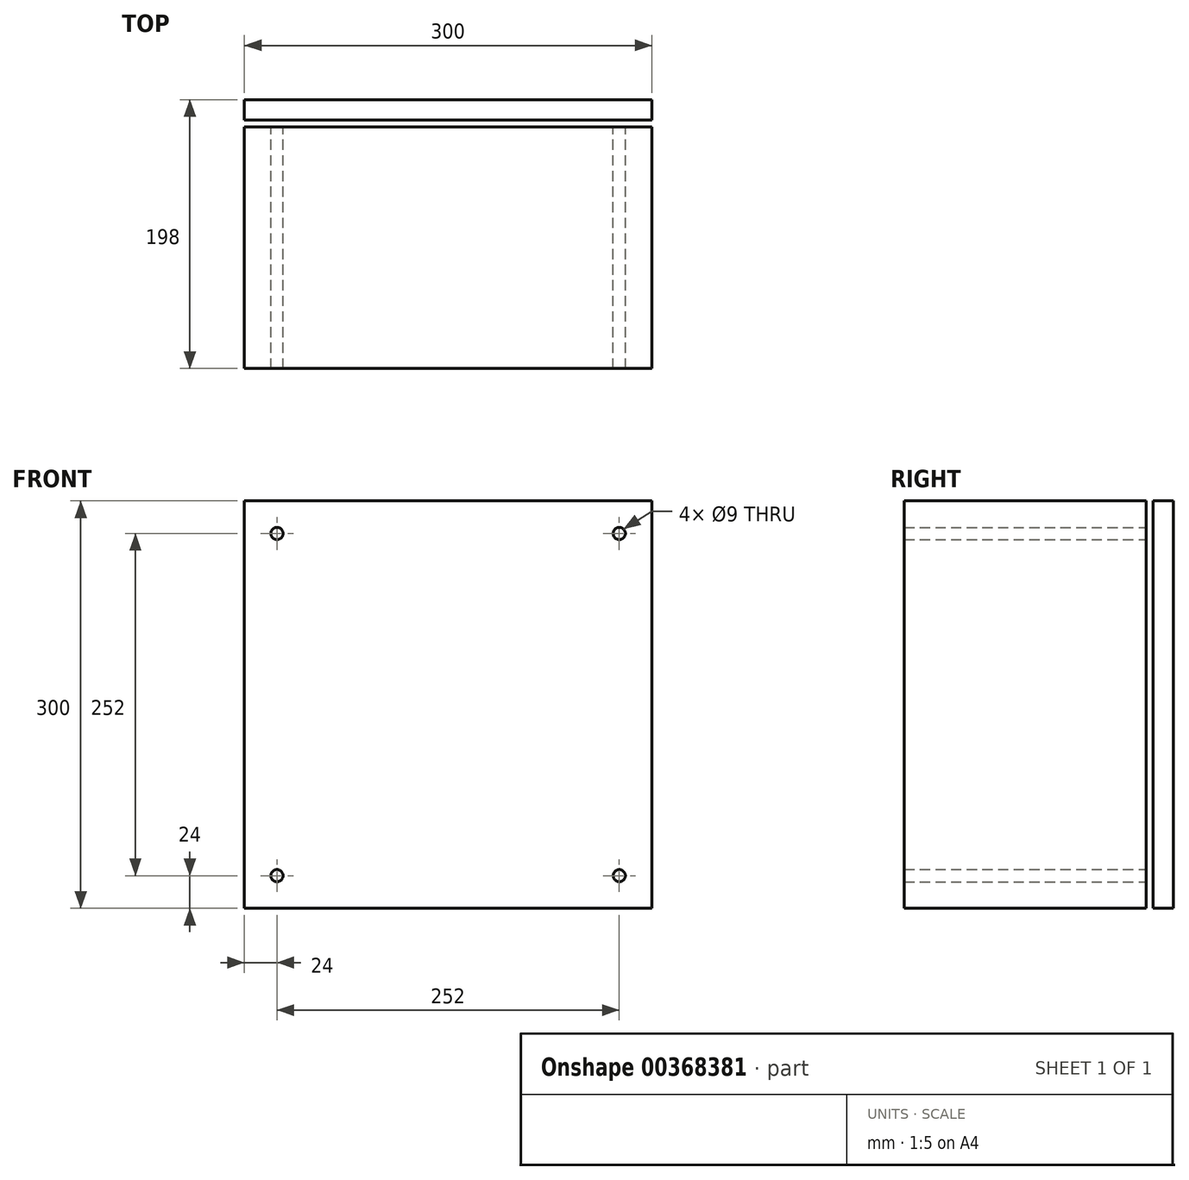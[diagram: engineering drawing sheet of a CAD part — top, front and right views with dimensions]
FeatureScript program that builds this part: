
annotation { "Feature Type Name" : "Feature", "Feature Type Description" : "" }
export const myFeature = defineFeature(function(context is Context, id is Id, definition is map)
    precondition{}
    {
        {
            var Q0;
            Q0=qCreatedBy(makeId("Front.planeOp"),FACE);
            var sketch = newSketch(context, id + "F0", { "sketchPlane" : qUnion([Q0])});
            skLineSegment(sketch, "E0.bottom", {"start": v(0, 0) * mm, "end": v(300, 0) * mm});
            skLineSegment(sketch, "E0.top", {"start": v(0, 300) * mm, "end": v(300, 300) * mm});
            skLineSegment(sketch, "E0.left", {"start": v(0, 0) * mm, "end": v(0, 300) * mm});
            skLineSegment(sketch, "E0.right", {"start": v(300, 0) * mm, "end": v(300, 300) * mm});
            skLineSegment(sketch, "E1", {"start": v(150, 300) * mm, "end": v(150, 0) * mm, "construction": true});
            skLineSegment(sketch, "E2", {"start": v(0, 150) * mm, "end": v(300, 150) * mm, "construction": true});
            skLineSegment(sketch, "E3.bottom", {"start": v(276, 24) * mm, "end": v(24, 24) * mm, "construction": true});
            skLineSegment(sketch, "E3.top", {"start": v(276, 276) * mm, "end": v(24, 276) * mm, "construction": true});
            skLineSegment(sketch, "E3.left", {"start": v(276, 24) * mm, "end": v(276, 276) * mm, "construction": true});
            skLineSegment(sketch, "E3.right", {"start": v(24, 24) * mm, "end": v(24, 276) * mm, "construction": true});
            skPoint(sketch, "E3.middle", {"position": v(150, 150) * mm});
            skCircle(sketch, "E4", {"center": v(24, 276) * mm, "radius": 4.5 * mm});
            skCircle(sketch, "E5", {"center": v(276, 276) * mm, "radius": 4.5 * mm});
            skCircle(sketch, "E6", {"center": v(276, 24) * mm, "radius": 4.5 * mm});
            skCircle(sketch, "E7", {"center": v(24, 24) * mm, "radius": 4.5 * mm});
            skSolve(sketch);
        }
        {
            var Q0;
            Q0 = qSketchRegion(id + "F0", true);
            extrude(context, id + "F1", {"entities" : qUnion([Q0]), "depth" : 178 * mm});
        }
        {
            var Q0;
            Q0=qCreatedBy(makeId("Right.planeOp"),FACE);
            var sketch = newSketch(context, id + "F2", { "sketchPlane" : qUnion([Q0])});
            skLineSegment(sketch, "E8.bottom", {"start": v(5, 0) * mm, "end": v(20, 0) * mm});
            skLineSegment(sketch, "E8.top", {"start": v(5, 300) * mm, "end": v(20, 300) * mm});
            skLineSegment(sketch, "E8.left", {"start": v(5, 0) * mm, "end": v(5, 300) * mm});
            skLineSegment(sketch, "E8.right", {"start": v(20, 0) * mm, "end": v(20, 300) * mm});
            skSolve(sketch);
        }
        {
            var Q0;
            Q0 = qSketchRegion(id + "F2", true);
            extrude(context, id + "F3", {"entities" : qUnion([Q0]), "depth" : 300 * mm});
        }
    });
